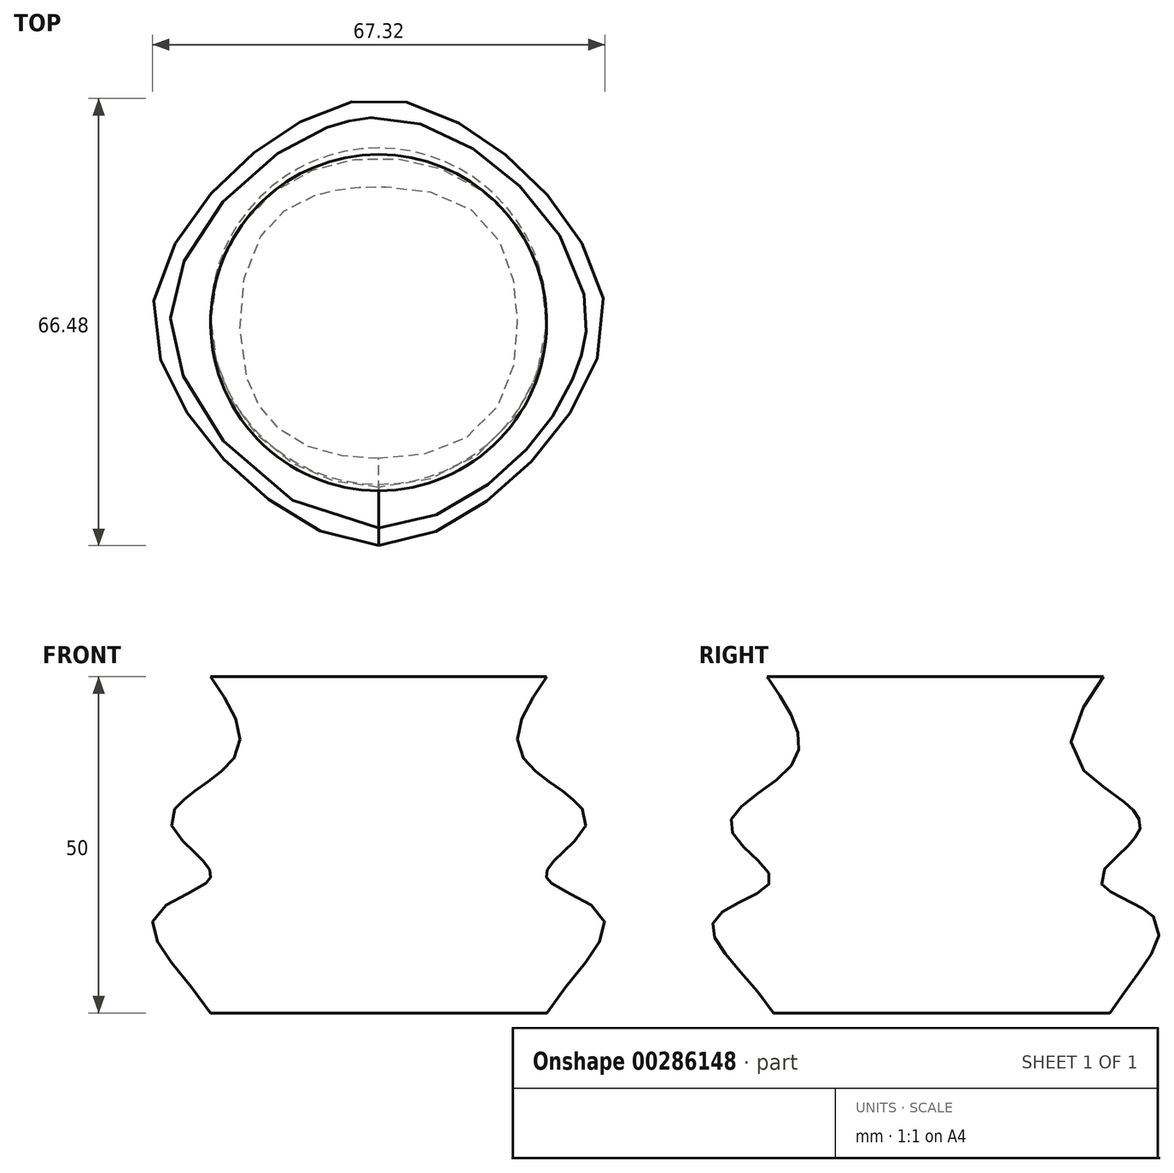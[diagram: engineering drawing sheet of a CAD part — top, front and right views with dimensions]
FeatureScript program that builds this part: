
annotation { "Feature Type Name" : "Feature", "Feature Type Description" : "" }
export const myFeature = defineFeature(function(context is Context, id is Id, definition is map)
    precondition{}
    {
        {
            var Q0;
            Q0=qCreatedBy(makeId("Top.planeOp"),FACE);
            cPlane(context, id + "F0", {"entities" : qUnion([Q0]), "cplaneType" : CPlaneType.OFFSET, "offset" : 50 * mm, "width" : 150 * mm, "height" : 150 * mm});
        }
        {
            var Q0;
            Q0=qCreatedBy(makeId("Top.planeOp"),FACE);
            var sketch = newSketch(context, id + "F1", { "sketchPlane" : qUnion([Q0])});
            skLineSegment(sketch, "E0.bottom", {"start": v(25, 25) * mm, "end": v(-25, 25) * mm});
            skLineSegment(sketch, "E0.top", {"start": v(25, -25) * mm, "end": v(-25, -25) * mm});
            skLineSegment(sketch, "E0.left", {"start": v(25, 25) * mm, "end": v(25, -25) * mm});
            skLineSegment(sketch, "E0.right", {"start": v(-25, 25) * mm, "end": v(-25, -25) * mm});
            skPoint(sketch, "E0.middle", {"position": v(0, 0) * mm});
            skCircle(sketch, "E1", {"center": v(0, 0) * mm, "radius": 25 * mm});
            skPoint(sketch, "E1.first.point", {"position": v(-1.33, 24.96) * mm});
            skPoint(sketch, "E1.second.point", {"position": v(0, -25) * mm});
            skPoint(sketch, "E1.third.point", {"position": v(25, 0) * mm});
            skSolve(sketch);
        }
        {
            var Q0;
            Q0=qCreatedBy(id+"F0.planeOp",FACE);
            var sketch = newSketch(context, id + "F2", { "sketchPlane" : qUnion([Q0])});
            skCircle(sketch, "E2", {"center": v(0, -0.95) * mm, "radius": 25 * mm});
            skSolve(sketch);
        }
        {
            var Q0;
            Q0=qCreatedBy(makeId("Right.planeOp"),FACE);
            var sketch = newSketch(context, id + "F3", { "sketchPlane" : qUnion([Q0])});
            skFitSpline(sketch, "E3", {"points": [v(25, 0) * mm, v(31.95, 13.77) * mm, v(23.54, 19.8) * mm, v(29.57, 27.82) * mm, v(19.97, 37.46) * mm, v(24.05, 50) * mm], "startDerivative": vector(47.52, 73.32) * mm, "endDerivative": vector(44.68, 65.89) * mm});
            skFitSpline(sketch, "E4.MirrorCS", {"points": [v(-25, 0) * mm, v(-33.85, 13.77) * mm, v(-25.45, 19.8) * mm, v(-31.47, 27.82) * mm, v(-21.87, 37.46) * mm, v(-25.95, 50) * mm], "startDerivative": vector(-47.52, 73.32) * mm, "endDerivative": vector(-44.68, 65.89) * mm});
            skSolve(sketch);
        }
        {
            var Q0;
            Q0=qCreatedBy(makeId("Front.planeOp"),FACE);
            var sketch = newSketch(context, id + "F4", { "sketchPlane" : qUnion([Q0])});
            skFitSpline(sketch, "E5.MirrorCS", {"points": [v(-25, 0) * mm, v(-33.33, 14.43) * mm, v(-24.93, 20.45) * mm, v(-30.95, 28.48) * mm, v(-21.35, 38.12) * mm, v(-24.98, 50) * mm], "startDerivative": vector(-47.52, 73.32) * mm, "endDerivative": vector(-44.68, 65.89) * mm});
            skFitSpline(sketch, "E6.MirrorCS", {"points": [v(25, 0) * mm, v(33.33, 14.43) * mm, v(24.93, 20.45) * mm, v(30.95, 28.48) * mm, v(21.35, 38.12) * mm, v(24.98, 50) * mm], "startDerivative": vector(47.52, 73.32) * mm, "endDerivative": vector(44.68, 65.89) * mm});
            skSolve(sketch);
        }
        {
            var Q0;
            {var subQ0=sQuery(id+"F1.wireOp",EDGE,"E1");var subQ1=makeQuery(id+"F1.imprint","INTERSECT",VERTEX,{"derivedFrom":[sQuery(id+"F1.wireOp",EDGE,"E0.bottom"),subQ0]});Q0=makeQuery(id+"F1.imprint","IMPRINT",FACE,{"disambiguationData":[TD([[makeQuery(id+"F1.imprint","IMPRINT",EDGE,{"disambiguationData":[TD([[subQ1,1.0]])],"derivedFrom":subQ0}),1.0]])]});}
            var Q1;
            Q1=makeQuery(id+"F2.imprint","IMPRINT",FACE,{"disambiguationData":[TD([[makeQuery(id+"F2.imprint","IMPRINT",EDGE,{"derivedFrom":sQuery(id+"F2.wireOp",EDGE,"E2")}),1.0]])]});
            var Q2;
            Q2=sQuery(id+"F3.wireOp",EDGE,"E3");
            var Q3;
            Q3=sQuery(id+"F3.wireOp",EDGE,"E4.MirrorCS");
            var Q4;
            Q4=sQuery(id+"F4.wireOp",EDGE,"E6.MirrorCS");
            var Q5;
            Q5=sQuery(id+"F4.wireOp",EDGE,"E5.MirrorCS");
            loft(context, id + "F5", {"addGuides" : true, "sheetProfilesArray" : [{ "sheetProfileEntities" : qUnion([Q0]) }, { "sheetProfileEntities" : qUnion([Q1]) }], "guidesArray" : [{ "guideEntities" : qUnion([Q2]), "guideDerivativeType" : LoftGuideDerivativeType.DEFAULT, "guideDerivativeMagnitude" : 1 }, { "guideEntities" : qUnion([Q3]), "guideDerivativeType" : LoftGuideDerivativeType.DEFAULT, "guideDerivativeMagnitude" : 1 }, { "guideEntities" : qUnion([Q4]), "guideDerivativeType" : LoftGuideDerivativeType.DEFAULT, "guideDerivativeMagnitude" : 1 }, { "guideEntities" : qUnion([Q5]), "guideDerivativeType" : LoftGuideDerivativeType.DEFAULT, "guideDerivativeMagnitude" : 1 }]});
        }
    });
